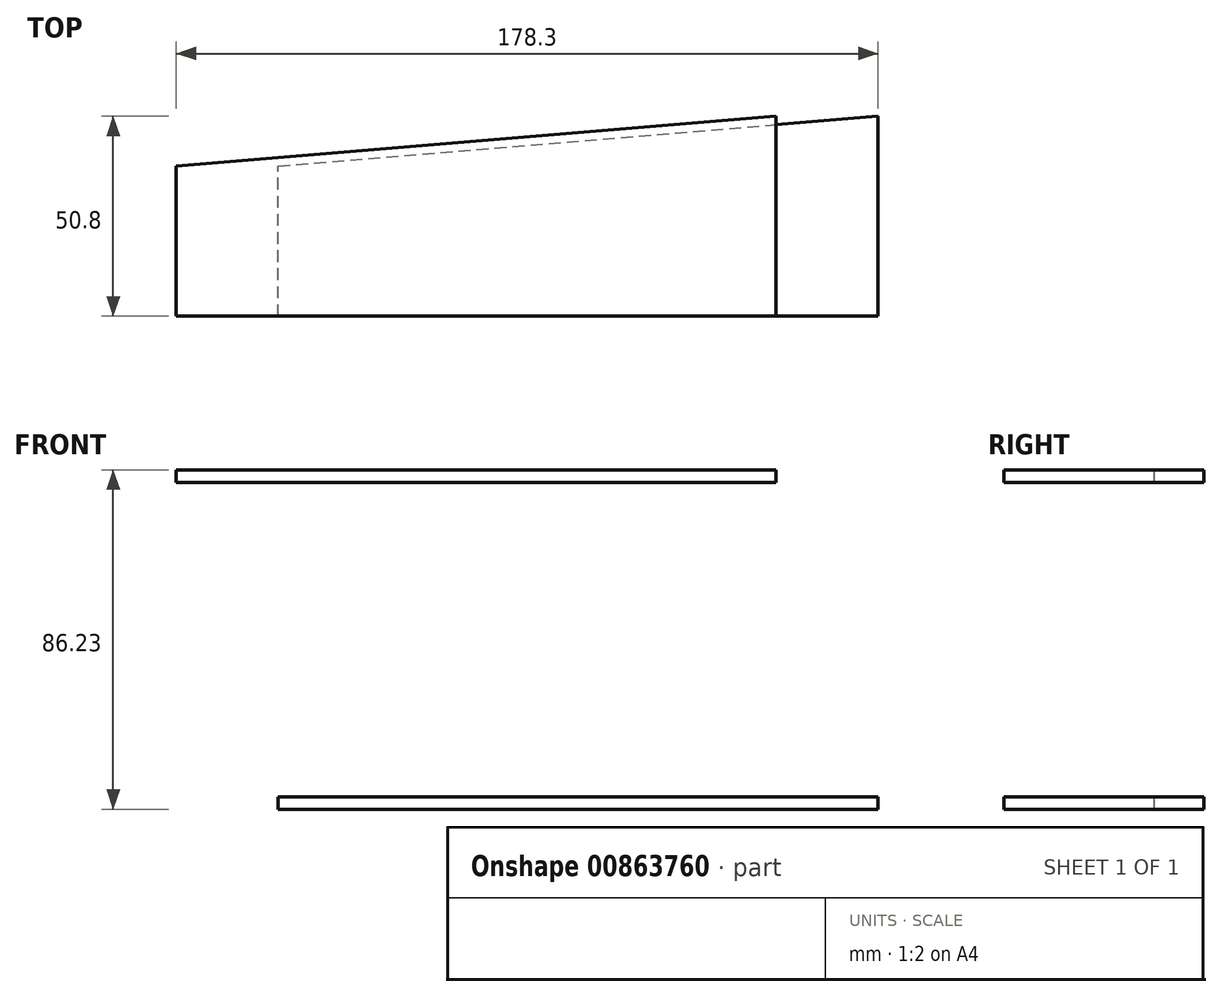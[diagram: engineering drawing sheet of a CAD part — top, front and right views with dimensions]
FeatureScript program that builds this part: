
annotation { "Feature Type Name" : "Feature", "Feature Type Description" : "" }
export const myFeature = defineFeature(function(context is Context, id is Id, definition is map)
    precondition{}
    {
        {
            var Q0;
            Q0=qCreatedBy(makeId("Top.planeOp"),FACE);
            var sketch = newSketch(context, id + "F0", { "sketchPlane" : qUnion([Q0])});
            skLineSegment(sketch, "E0.bottom", {"start": v(-144.5, -6.08) * mm, "end": v(160.3, -6.08) * mm});
            skLineSegment(sketch, "E0.left", {"start": v(-144.5, -6.08) * mm, "end": v(-144.5, 32.02) * mm});
            skLineSegment(sketch, "E0.right", {"start": v(160.3, -6.08) * mm, "end": v(160.3, 32.02) * mm});
            skLineSegment(sketch, "E1", {"start": v(7.9, 44.72) * mm, "end": v(7.9, -6.08) * mm});
            skPoint(sketch, "E2", {"position": v(-144.5, 32.02) * mm});
            skPoint(sketch, "E3", {"position": v(160.3, 32.02) * mm});
            skLineSegment(sketch, "E4", {"start": v(-144.5, 32.02) * mm, "end": v(7.9, 44.72) * mm});
            skLineSegment(sketch, "E5", {"start": v(160.3, 32.02) * mm, "end": v(7.9, 44.72) * mm});
            skPoint(sketch, "E6.orphan", {"position": v(-144.5, 44.72) * mm});
            skPoint(sketch, "E7.orphan", {"position": v(160.3, 44.72) * mm});
            skSolve(sketch);
        }
        {
            var Q0;
            {var subQ0=sQuery(id+"F0.wireOp",EDGE,"E0.left");Q0=makeQuery(id+"F0.imprint","IMPRINT",FACE,{"disambiguationData":[TD([[makeQuery(id+"F0.imprint","IMPRINT",EDGE,{"derivedFrom":subQ0}),-1.0]])]});}
            extrude(context, id + "F1", {"entities" : qUnion([Q0]), "depth" : 3.17 * mm, "offsetDistance" : 25.4 * mm});
        }
        {
            var Q0;
            Q0=makeQuery(id+"F1.opExtrude","SWEPT_BODY",BODY,{"disambiguationData":[OSD([sQuery(id+"F0.wireOp",EDGE,"E0.bottom"),sQuery(id+"F0.wireOp",EDGE,"E0.left"),sQuery(id+"F0.wireOp",EDGE,"E1"),sQuery(id+"F0.wireOp",EDGE,"E4")])]});
            transform(context, id + "F2", {"entities" : qUnion([Q0]), "transformType" : TransformType.TRANSLATION_3D, "dx" : -25.9 * mm, "dy" : 0 * mm, "dz" : 83.06 * mm, "makeCopy" : true});
        }
    });
